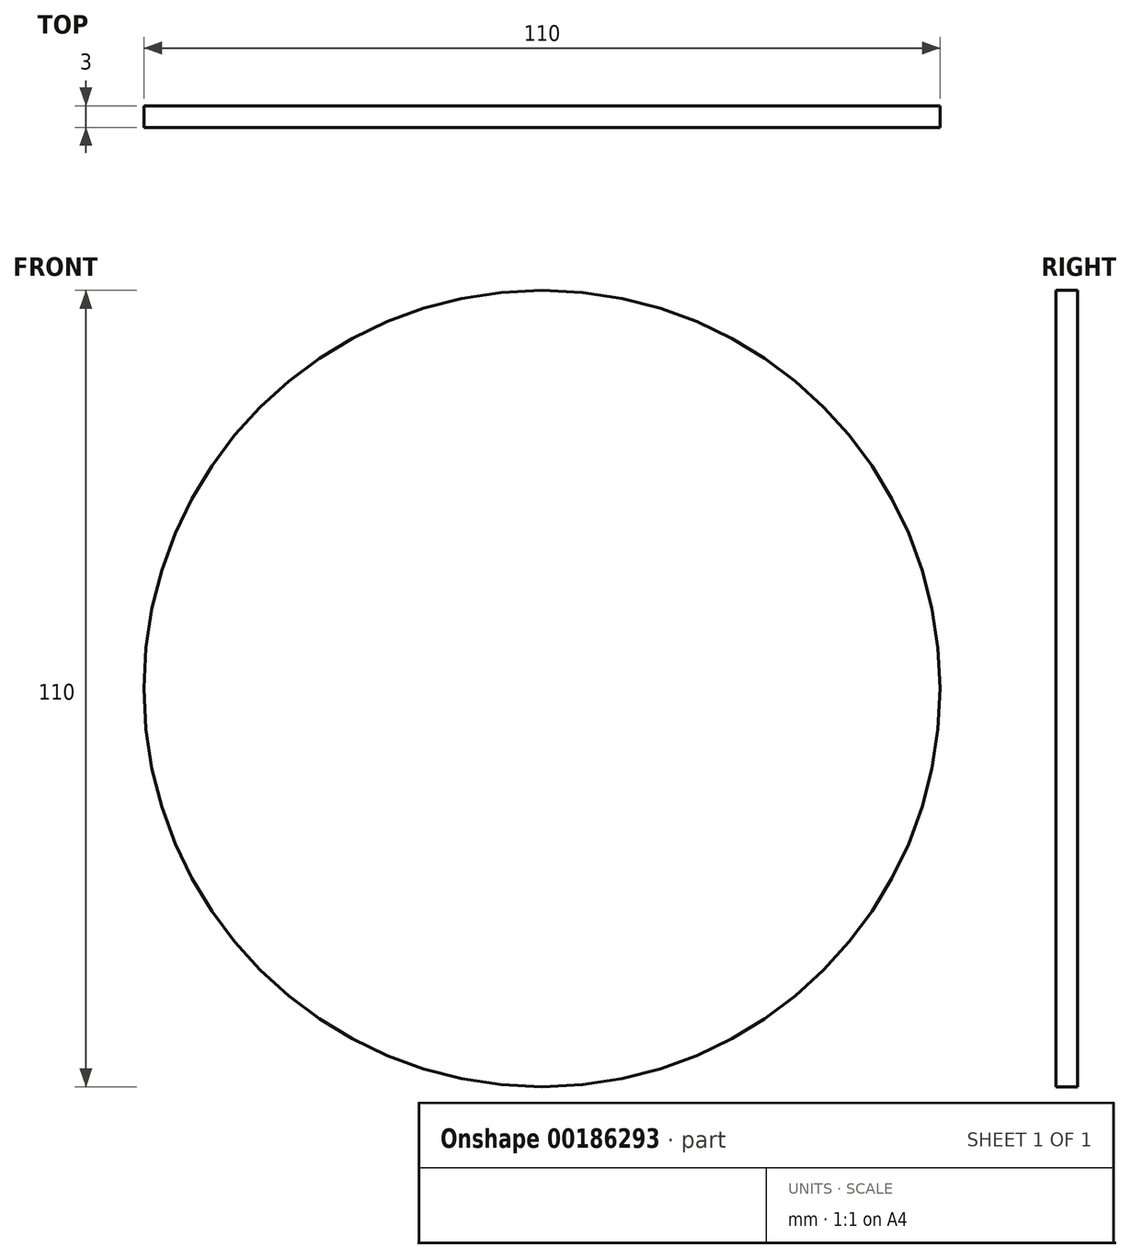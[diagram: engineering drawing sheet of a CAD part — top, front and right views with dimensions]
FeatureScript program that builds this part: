
annotation { "Feature Type Name" : "Feature", "Feature Type Description" : "" }
export const myFeature = defineFeature(function(context is Context, id is Id, definition is map)
    precondition{}
    {
        {
            var Q0;
            Q0=qCreatedBy(makeId("Front.planeOp"),FACE);
            var sketch = newSketch(context, id + "F0", { "sketchPlane" : qUnion([Q0])});
            skCircle(sketch, "E0", {"center": v(0, 0) * mm, "radius": 55 * mm});
            skSolve(sketch);
        }
        {
            var Q0;
            Q0 = qSketchRegion(id + "F0", true);
            extrude(context, id + "F1", {"entities" : qUnion([Q0]), "depth" : 3 * mm});
        }
    });
